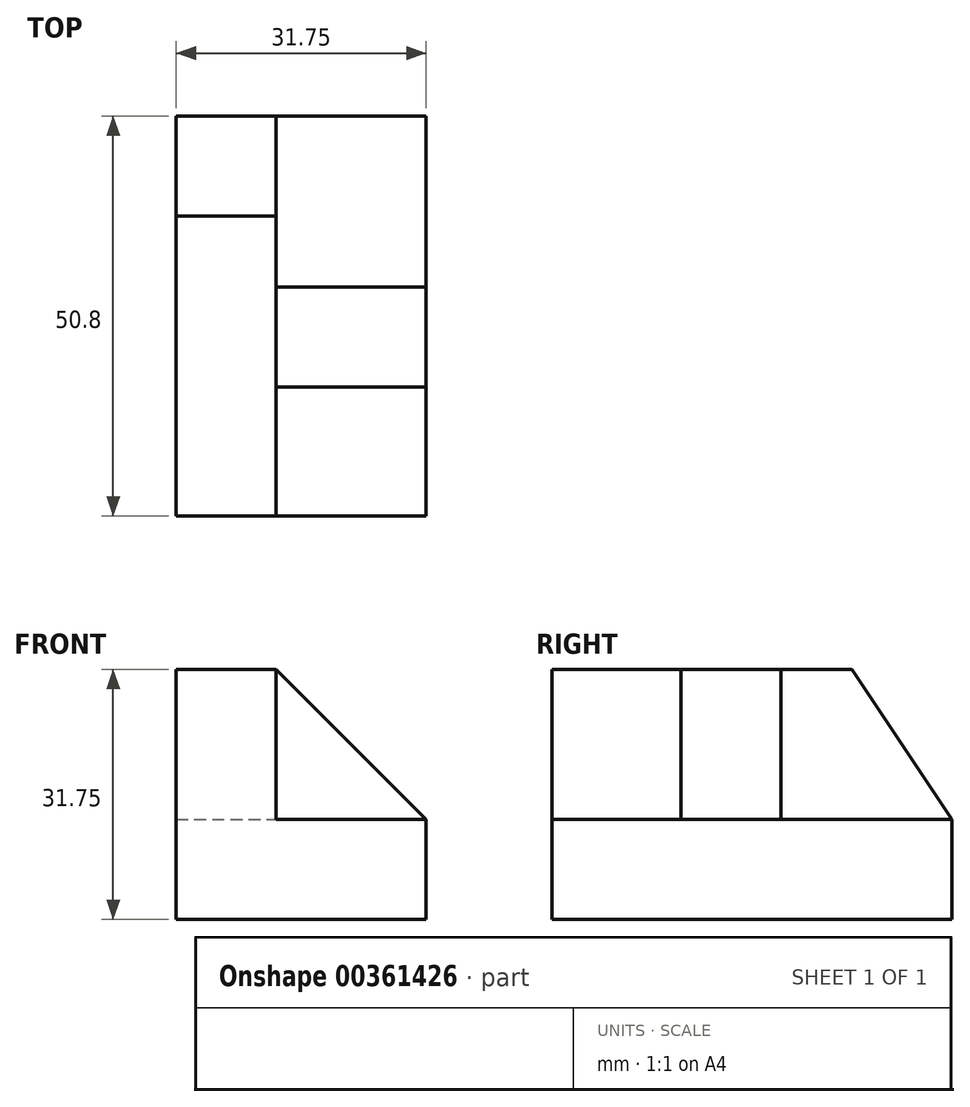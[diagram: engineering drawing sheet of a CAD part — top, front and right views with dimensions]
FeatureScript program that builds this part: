
annotation { "Feature Type Name" : "Feature", "Feature Type Description" : "" }
export const myFeature = defineFeature(function(context is Context, id is Id, definition is map)
    precondition{}
    {
        {
            var Q0;
            Q0=qCreatedBy(makeId("Top.planeOp"),FACE);
            var sketch = newSketch(context, id + "F0", { "sketchPlane" : qUnion([Q0])});
            skLineSegment(sketch, "E0", {"start": v(0, 0) * mm, "end": v(0, 50.8) * mm});
            skLineSegment(sketch, "E1", {"start": v(0, 50.8) * mm, "end": v(31.75, 50.8) * mm});
            skLineSegment(sketch, "E2", {"start": v(31.75, 50.8) * mm, "end": v(31.75, 0) * mm});
            skLineSegment(sketch, "E3", {"start": v(31.75, 0) * mm, "end": v(0, 0) * mm});
            skSolve(sketch);
        }
        {
            var Q0;
            Q0 = qSketchRegion(id + "F0", true);
            extrude(context, id + "F1", {"entities" : qUnion([Q0]), "depth" : 12.7 * mm});
        }
        {
            var Q0;
            Q0=makeQuery(id+"F1.opExtrude","CAP_FACE",FACE,{"disambiguationData":[OSD([sQuery(id+"F0.wireOp",EDGE,"E0"),sQuery(id+"F0.wireOp",EDGE,"E1"),sQuery(id+"F0.wireOp",EDGE,"E2"),sQuery(id+"F0.wireOp",EDGE,"E3")])],"isStart":false});
            var sketch = newSketch(context, id + "F2", { "sketchPlane" : qUnion([Q0])});
            skLineSegment(sketch, "E4", {"start": v(0, 50.8) * mm, "end": v(12.7, 50.8) * mm});
            skLineSegment(sketch, "E5", {"start": v(12.7, 50.8) * mm, "end": v(12.7, 0) * mm});
            skLineSegment(sketch, "E6", {"start": v(12.7, 0) * mm, "end": v(0, 0) * mm});
            skLineSegment(sketch, "E7", {"start": v(0, 0) * mm, "end": v(0, 50.8) * mm});
            skSolve(sketch);
        }
        {
            var Q0;
            Q0 = qSketchRegion(id + "F2", true);
            extrude(context, id + "F3", {"entities" : qUnion([Q0]), "operationType" : NewBodyOperationType.ADD, "depth" : 19.05 * mm});
        }
        {
            var Q0;
            Q0=makeQuery(id+"F3.opExtrude","SWEPT_FACE",FACE,{"disambiguationData":[OSD([sQuery(id+"F2.wireOp",EDGE,"E5")])]});
            var sketch = newSketch(context, id + "F4", { "sketchPlane" : qUnion([Q0])});
            skLineSegment(sketch, "E8", {"start": v(50.8, 31.75) * mm, "end": v(50.8, 12.7) * mm});
            skLineSegment(sketch, "E9", {"start": v(50.8, 12.7) * mm, "end": v(38.1, 31.75) * mm});
            skLineSegment(sketch, "E10", {"start": v(38.1, 31.75) * mm, "end": v(50.8, 31.75) * mm});
            skSolve(sketch);
        }
        {
            var Q0;
            Q0 = qSketchRegion(id + "F4", true);
            extrude(context, id + "F5", {"entities" : qUnion([Q0]), "operationType" : NewBodyOperationType.REMOVE, "oppositeDirection" : true, "depth" : 25.4 * mm});
        }
        {
            var Q0;
            Q0=makeQuery(id+"F3.opExtrude","SWEPT_FACE",FACE,{"disambiguationData":[OSD([sQuery(id+"F2.wireOp",EDGE,"E5")])]});
            var sketch = newSketch(context, id + "F6", { "sketchPlane" : qUnion([Q0])});
            skLineSegment(sketch, "E11", {"start": v(16.35, 31.75) * mm, "end": v(16.35, 12.7) * mm});
            skLineSegment(sketch, "E12", {"start": v(16.35, 12.7) * mm, "end": v(29.05, 12.7) * mm});
            skLineSegment(sketch, "E13", {"start": v(29.05, 12.7) * mm, "end": v(29.05, 31.75) * mm});
            skLineSegment(sketch, "E14", {"start": v(29.05, 31.75) * mm, "end": v(16.35, 31.75) * mm});
            skSolve(sketch);
        }
        {
            var Q0;
            Q0 = qSketchRegion(id + "F6", true);
            extrude(context, id + "F7", {"entities" : qUnion([Q0]), "operationType" : NewBodyOperationType.ADD, "depth" : 19.05 * mm});
        }
        {
            var Q0;
            Q0=makeQuery(id+"F7.opExtrude","SWEPT_FACE",FACE,{"disambiguationData":[OSD([sQuery(id+"F6.wireOp",EDGE,"E11")])]});
            var sketch = newSketch(context, id + "F8", { "sketchPlane" : qUnion([Q0])});
            skLineSegment(sketch, "E15", {"start": v(31.75, 31.75) * mm, "end": v(31.75, 12.7) * mm});
            skLineSegment(sketch, "E16", {"start": v(31.75, 12.7) * mm, "end": v(12.7, 31.75) * mm});
            skLineSegment(sketch, "E17", {"start": v(12.7, 31.75) * mm, "end": v(31.75, 31.75) * mm});
            skSolve(sketch);
        }
        {
            var Q0;
            Q0 = qSketchRegion(id + "F8", true);
            extrude(context, id + "F9", {"entities" : qUnion([Q0]), "operationType" : NewBodyOperationType.REMOVE, "oppositeDirection" : true, "depth" : 25.4 * mm});
        }
    });
